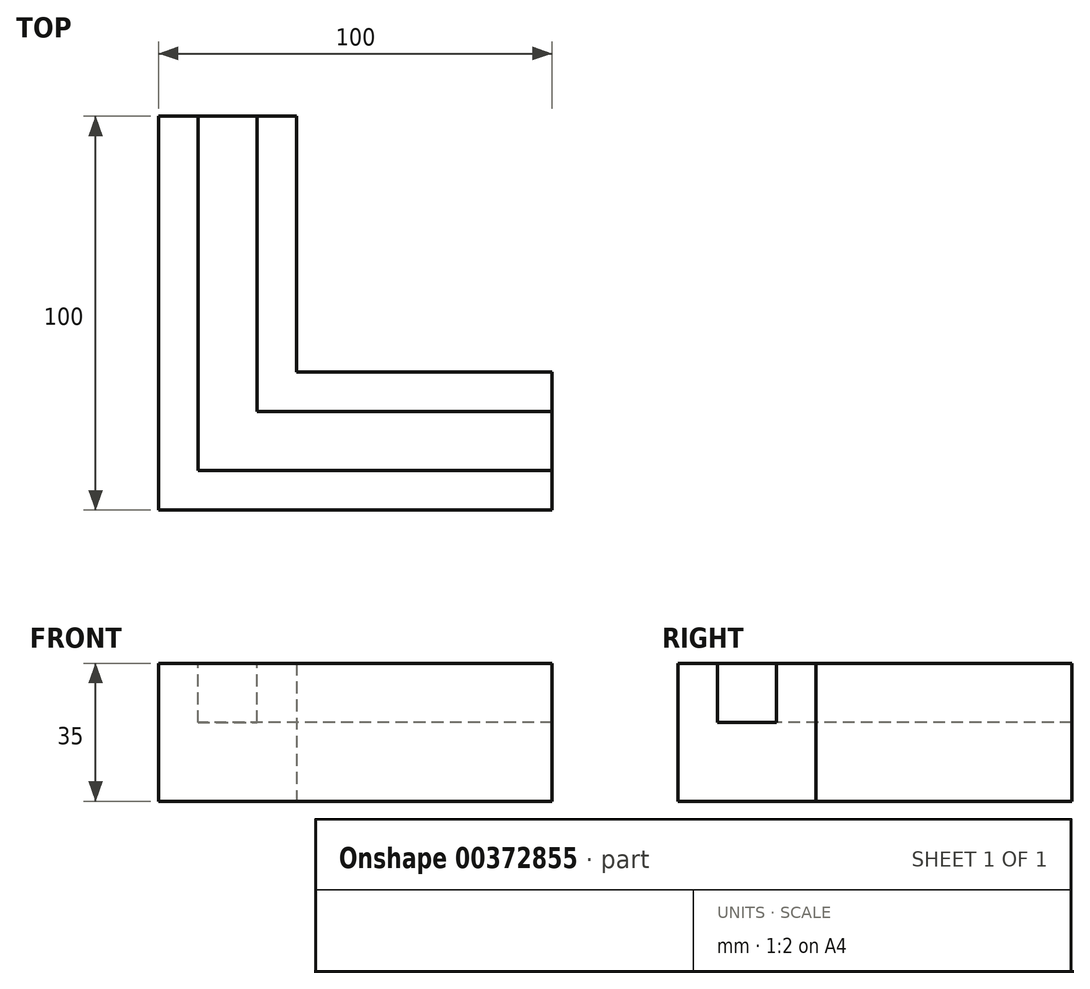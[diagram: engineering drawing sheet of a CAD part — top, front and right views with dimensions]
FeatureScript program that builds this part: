
annotation { "Feature Type Name" : "Feature", "Feature Type Description" : "" }
export const myFeature = defineFeature(function(context is Context, id is Id, definition is map)
    precondition{}
    {
        {
            var Q0;
            Q0=qCreatedBy(makeId("Top.planeOp"),FACE);
            var sketch = newSketch(context, id + "F0", { "sketchPlane" : qUnion([Q0])});
            skLineSegment(sketch, "E0", {"start": v(0, 100) * mm, "end": v(0, 0) * mm});
            skLineSegment(sketch, "E1", {"start": v(0, 0) * mm, "end": v(100, 0) * mm});
            skLineSegment(sketch, "E2", {"start": v(0, 100) * mm, "end": v(35, 100) * mm});
            skLineSegment(sketch, "E3", {"start": v(35, 100) * mm, "end": v(35, 35) * mm});
            skLineSegment(sketch, "E4", {"start": v(35, 35) * mm, "end": v(100, 35) * mm});
            skLineSegment(sketch, "E5", {"start": v(100, 35) * mm, "end": v(100, 0) * mm});
            skLineSegment(sketch, "E6", {"start": v(17.5, 100) * mm, "end": v(17.5, 17.5) * mm, "construction": true});
            skLineSegment(sketch, "E7", {"start": v(17.5, 17.5) * mm, "end": v(100, 17.5) * mm, "construction": true});
            skSolve(sketch);
        }
        {
            var Q0;
            Q0 = qSketchRegion(id + "F0", true);
            extrude(context, id + "F1", {"entities" : qUnion([Q0]), "depth" : 35 * mm});
        }
        {
            var Q0;
            Q0=makeQuery(id+"F1.opExtrude","CAP_FACE",FACE,{"disambiguationData":[OSD([sQuery(id+"F0.wireOp",EDGE,"E0"),sQuery(id+"F0.wireOp",EDGE,"E1"),sQuery(id+"F0.wireOp",EDGE,"E2"),sQuery(id+"F0.wireOp",EDGE,"E3"),sQuery(id+"F0.wireOp",EDGE,"E4"),sQuery(id+"F0.wireOp",EDGE,"E5")])],"isStart":false});
            var sketch = newSketch(context, id + "F2", { "sketchPlane" : qUnion([Q0])});
            skLineSegment(sketch, "E8", {"start": v(17.5, 100) * mm, "end": v(17.5, 17.5) * mm, "construction": true});
            skLineSegment(sketch, "E9", {"start": v(100, 17.5) * mm, "end": v(17.5, 17.5) * mm, "construction": true});
            skLineSegment(sketch, "E10.0", {"start": v(10, 100) * mm, "end": v(10, 10) * mm});
            skLineSegment(sketch, "E11.0", {"start": v(100, 10) * mm, "end": v(10, 10) * mm});
            skLineSegment(sketch, "E12.MirrorCS", {"start": v(100, 25) * mm, "end": v(25, 25) * mm});
            skLineSegment(sketch, "E13.MirrorCS", {"start": v(25, 100) * mm, "end": v(25, 25) * mm});
            skPoint(sketch, "E14.orphan", {"position": v(10, 25) * mm});
            skPoint(sketch, "E15.trimOffspring.end.orphan", {"position": v(25, 10) * mm});
            skLineSegment(sketch, "E16", {"start": v(10, 100) * mm, "end": v(25, 100) * mm});
            skLineSegment(sketch, "E17", {"start": v(100, 25) * mm, "end": v(100, 10) * mm});
            skSolve(sketch);
        }
        {
            var Q0;
            Q0 = qSketchRegion(id + "F2", true);
            extrude(context, id + "F3", {"entities" : qUnion([Q0]), "operationType" : NewBodyOperationType.REMOVE, "oppositeDirection" : true, "depth" : 15 * mm});
        }
    });
